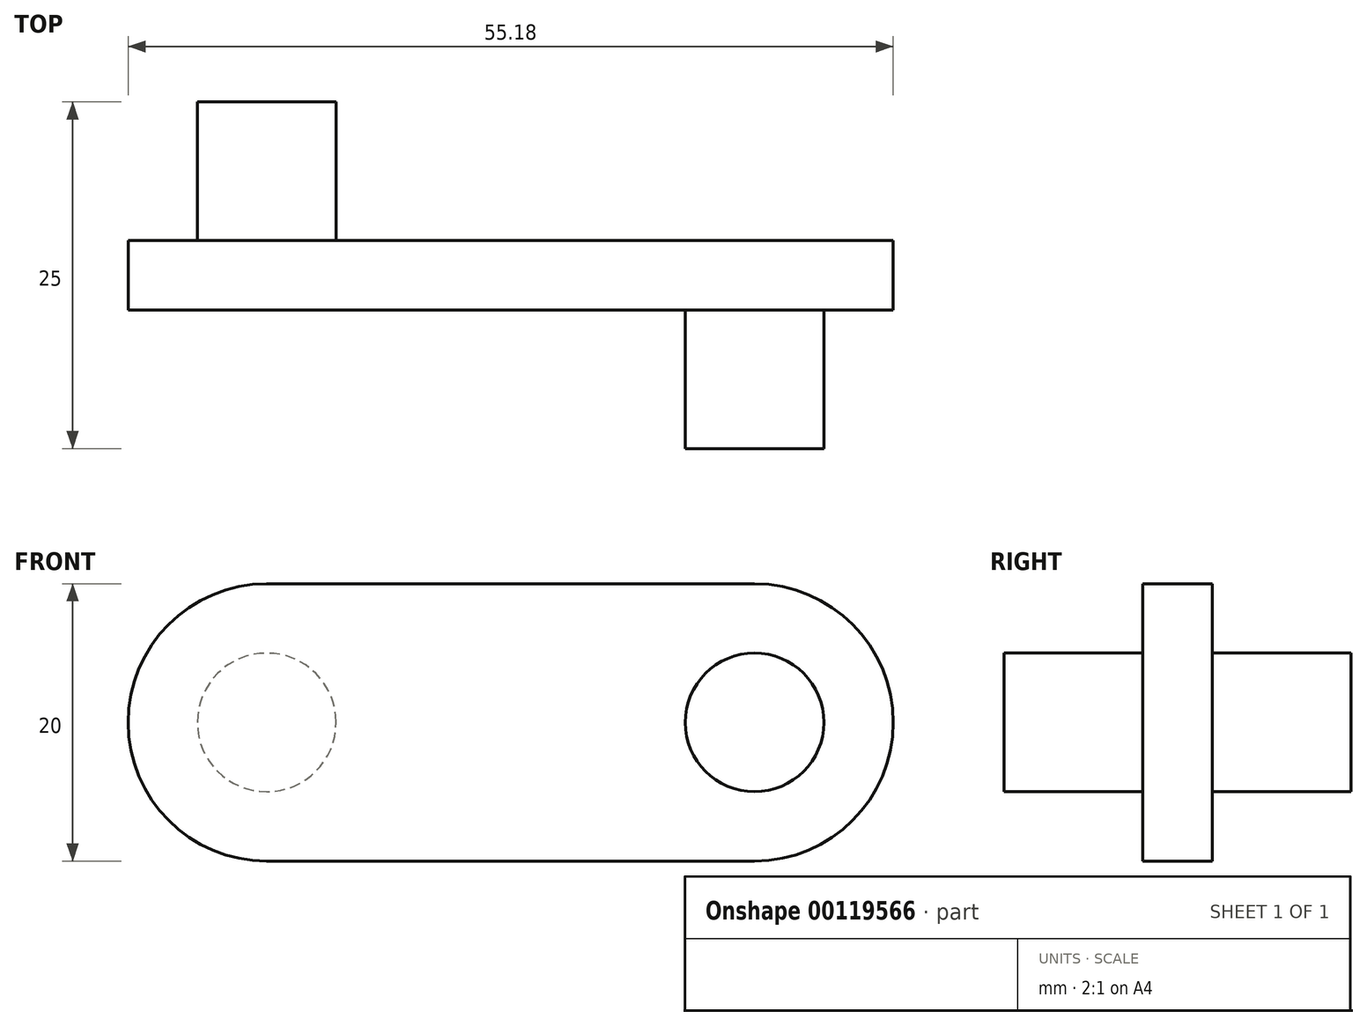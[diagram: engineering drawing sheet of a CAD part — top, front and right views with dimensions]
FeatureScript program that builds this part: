
annotation { "Feature Type Name" : "Feature", "Feature Type Description" : "" }
export const myFeature = defineFeature(function(context is Context, id is Id, definition is map)
    precondition{}
    {
        {
            var Q0;
            Q0=qCreatedBy(makeId("Front.planeOp"),FACE);
            var sketch = newSketch(context, id + "F0", { "sketchPlane" : qUnion([Q0])});
            skLineSegment(sketch, "E0", {"start": v(0, 0) * mm, "end": v(35.18, 0) * mm});
            skArc(sketch, "E1", {"start": v(35.18, 0) * mm, "mid": v(45.18, -10) * mm, "end": v(35.18, -20) * mm});
            skLineSegment(sketch, "E2", {"start": v(35.18, -20) * mm, "end": v(0, -20) * mm});
            skArc(sketch, "E3", {"start": v(0, -20) * mm, "mid": v(-10, -10) * mm, "end": v(0, 0) * mm});
            skCircle(sketch, "E4", {"center": v(0, -10) * mm, "radius": 5 * mm});
            skCircle(sketch, "E5", {"center": v(35.18, -10) * mm, "radius": 5 * mm});
            skSolve(sketch);
        }
        {
            var Q0;
            Q0 = qSketchRegion(id + "F0", true);
            extrude(context, id + "F1", {"entities" : qUnion([Q0]), "depth" : 5 * mm});
        }
        {
            var Q0;
            Q0=makeQuery(id+"F0.imprint","IMPRINT",FACE,{"disambiguationData":[TD([[makeQuery(id+"F0.imprint","IMPRINT",EDGE,{"derivedFrom":sQuery(id+"F0.wireOp",EDGE,"E5")}),1.0]])]});
            extrude(context, id + "F2", {"entities" : qUnion([Q0]), "operationType" : NewBodyOperationType.ADD, "depth" : 15 * mm});
        }
        {
            var Q0;
            Q0=makeQuery(id+"F0.imprint","IMPRINT",FACE,{"disambiguationData":[TD([[makeQuery(id+"F0.imprint","IMPRINT",EDGE,{"derivedFrom":sQuery(id+"F0.wireOp",EDGE,"E4")}),1.0]])]});
            var Q1;
            Q1=makeQuery(id+"F1.opExtrude","CAP_FACE",FACE,{"disambiguationData":[OSD([sQuery(id+"F0.wireOp",EDGE,"E0"),sQuery(id+"F0.wireOp",EDGE,"E1"),sQuery(id+"F0.wireOp",EDGE,"E2"),sQuery(id+"F0.wireOp",EDGE,"E3"),sQuery(id+"F0.wireOp",EDGE,"E4"),sQuery(id+"F0.wireOp",EDGE,"E5")])],"isStart":false});
            extrude(context, id + "F3", {"entities" : qUnion([Q0]), "operationType" : NewBodyOperationType.ADD, "oppositeDirection" : true, "depth" : 10 * mm, "hasSecondDirection" : true, "secondDirectionBound" : SecondDirectionBoundingType.UP_TO_SURFACE, "secondDirectionOppositeDirection" : false, "secondDirectionBoundEntityFace" : qUnion([Q1]), "secondDirectionDepth" : 5 * mm});
        }
    });
